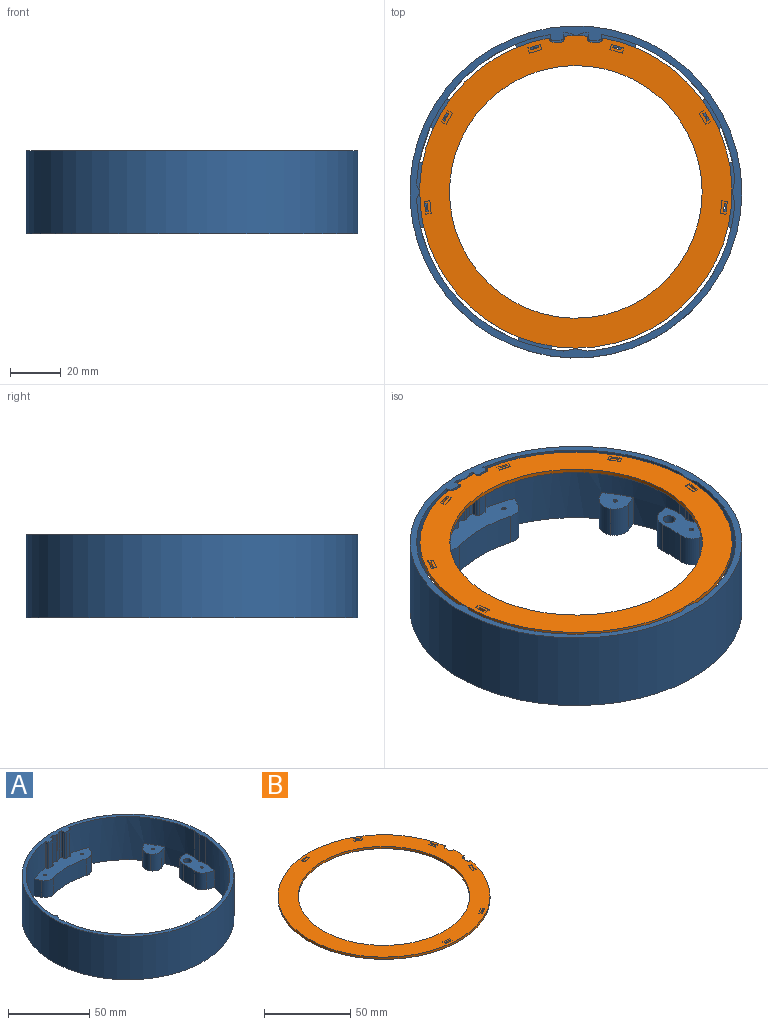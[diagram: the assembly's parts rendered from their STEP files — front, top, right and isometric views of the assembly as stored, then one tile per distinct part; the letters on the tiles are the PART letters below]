
ASSEMBLY  parts=2 mates=1
PART A: 74 faces, bbox 130.8x130.8x32.6 mm
  f0: cylinder r=62.87mm len=57.25mm, axis (0,0,1), area 2296.4mm2, adj f1,f5,f8,f10,f27,f44,f45,f46
  f1: plane 25.87x10.33mm, normal (0,0,1), area 199.3mm2, adj f0,f3,f15,f19,f34,f36,f47,f48
  f2: plane 25.87x10.43mm, normal (0,0,1), area 200.9mm2, adj f3,f4,f12,f22,f35,f38,f41,f55
  f3: cylinder r=62.87mm len=125.47mm, axis (0,0,1), area 5557.1mm2, adj f1,f2,f10,f13,f36,f37,f38,f39
  f4: cylinder r=62.87mm len=58.91mm, axis (0,0,1), area 2329.4mm2, adj f2,f5,f9,f10,f24,f40,f41,f42
  f5: plane 47.77x12.29mm, normal (0,0,1), area 400.8mm2, adj f0,f4,f6,f7,f11,f17,f20,f24
  f6: cylinder r=62.87mm len=19.94mm, axis (0,0,1), area 33.8mm2, adj f5,f25,f60,f73
  f7: cylinder r=62.87mm len=19.94mm, axis (0,0,1), area 33.8mm2, adj f5,f28,f60,f72
  f8: plane 13.34x12.6mm, normal (0,0,1), area 105.4mm2, adj f0,f23,f45,f46,f49,f50
  f9: plane 13.34x12.6mm, normal (0,0,1), area 105.4mm2, adj f4,f21,f40,f42,f52,f53
  f10: plane 130.81x130.81mm, normal (0,0,-1), area 2194.9mm2, adj f0,f3,f4,f11,f12,f14,f15,f16
  f11: cylinder r=52.7mm len=28.54mm, axis (0,0,-1), area 366.3mm2, adj f5,f10,f51,f54
  f12: cylinder r=52.7mm len=12.67mm, axis (0,0,-1), area 126.7mm2, adj f2,f10,f55,f59
  f13: plane 14.43x11.55mm, normal (0,0,1), area 118.3mm2, adj f3,f14,f18,f37,f39,f57,f58
  f14: cylinder r=52.7mm len=12.67mm, axis (0,0,-1), area 11.7mm2, adj f10,f13,f57,f58
  f15: cylinder r=52.7mm len=12.67mm, axis (0,0,-1), area 126.7mm2, adj f1,f10,f48,f56
  f16: cylinder r=65.41mm len=130.81mm, axis (0,0,-1), area 13402.6mm2, adj f10,f60
  f17: cylinder r=0.83mm len=12.67mm, axis (0,0,1), area 65.7mm2, adj f5,f10
  f18: cylinder r=0.83mm len=12.67mm, axis (0,0,1), area 65.7mm2, adj f10,f13
  f19: cylinder r=0.83mm len=12.67mm, axis (0,0,1), area 65.7mm2, adj f1,f10
  f20: cylinder r=0.83mm len=12.67mm, axis (0,0,1), area 65.7mm2, adj f5,f10
  f21: cylinder r=0.83mm len=12.67mm, axis (0,0,1), area 65.7mm2, adj f9,f10
  f22: cylinder r=0.83mm len=12.67mm, axis (0,0,1), area 65.7mm2, adj f2,f10
  f23: cylinder r=0.83mm len=12.67mm, axis (0,0,1), area 65.7mm2, adj f8,f10
  f24: plane 19.94x1.21mm, normal (-1,0,0), area 24mm2, adj f4,f5,f33,f60
  f25: plane 19.94x1.85mm, normal (1,0,0), area 36.8mm2, adj f5,f6,f32,f60
  f26: plane 19.94x3.3mm, normal (0,-1,0), area 65.8mm2, adj f5,f32,f33,f60
  f27: plane 19.94x1.21mm, normal (1,0,0), area 24mm2, adj f0,f5,f31,f60
  f28: plane 19.94x1.85mm, normal (-1,0,0), area 36.8mm2, adj f5,f7,f30,f60
  f29: plane 19.94x3.3mm, normal (0,-1,0), area 65.8mm2, adj f5,f30,f31,f60
  f30: cylinder r=1.02mm len=19.94mm, axis (0,0,1), area 31.8mm2, adj f5,f28,f29,f60
  f31: cylinder r=1.02mm len=19.94mm, axis (0,0,-1), area 31.8mm2, adj f5,f27,f29,f60
  f32: cylinder r=1.02mm len=19.94mm, axis (0,0,1), area 31.8mm2, adj f5,f25,f26,f60
  f33: cylinder r=1.02mm len=19.94mm, axis (0,0,-1), area 31.8mm2, adj f5,f24,f26,f60
  f34: cylinder r=2.35mm len=12.67mm, axis (0,0,1), area 187.1mm2, adj f1,f10
  f35: cylinder r=2.35mm len=12.67mm, axis (0,0,1), area 187.1mm2, adj f2,f10
  f36: plane 12.67x4.78mm, normal (-0.35,-0.94,0), area 64.7mm2, adj f1,f3,f10,f56
  f37: plane 12.67x2.99mm, normal (0.95,-0.31,0), area 39.8mm2, adj f3,f10,f13,f57
  f38: plane 12.67x4.78mm, normal (0.35,-0.94,0), area 64.7mm2, adj f2,f3,f10,f59
  f39: plane 12.67x3.41mm, normal (-0.96,0.28,0), area 44.9mm2, adj f3,f10,f13,f58
  f40: plane 12.67x4.16mm, normal (-0.36,-0.93,0), area 56.6mm2, adj f4,f9,f10,f52
  f41: plane 12.67x4mm, normal (0.17,0.98,0), area 51.4mm2, adj f2,f4,f10,f55
  f42: plane 12.67x3.16mm, normal (0.53,0.85,0), area 47.4mm2, adj f4,f9,f10,f53
  f43: plane 12.67x4.29mm, normal (-0.88,-0.47,0), area 61.7mm2, adj f4,f5,f10,f54
  f44: plane 12.67x4.29mm, normal (0.88,-0.47,0), area 61.7mm2, adj f0,f5,f10,f51
  f45: plane 12.67x3.16mm, normal (-0.53,0.85,0), area 47.4mm2, adj f0,f8,f10,f49
  f46: plane 12.67x4.16mm, normal (0.36,-0.93,0), area 56.6mm2, adj f0,f8,f10,f50
  f47: plane 12.67x4mm, normal (-0.17,0.98,0), area 51.4mm2, adj f0,f1,f10,f48
  f48: cylinder r=6.35mm len=12.67mm, axis (0,0,-1), area 119mm2, adj f1,f10,f15,f47
  f49: cylinder r=6.35mm len=12.67mm, axis (0,0,-1), area 120.7mm2, adj f8,f10,f45,f50
  f50: cylinder r=6.35mm len=12.67mm, axis (0,0,-1), area 111.4mm2, adj f8,f10,f46,f49
  f51: cylinder r=6.35mm len=12.67mm, axis (0,0,-1), area 109mm2, adj f5,f10,f11,f44
  f52: cylinder r=6.35mm len=12.67mm, axis (0,0,-1), area 111.4mm2, adj f9,f10,f40,f53
  f53: cylinder r=6.35mm len=12.67mm, axis (0,0,-1), area 120.7mm2, adj f9,f10,f42,f52
  f54: cylinder r=6.35mm len=12.67mm, axis (0,0,-1), area 109mm2, adj f5,f10,f11,f43
  f55: cylinder r=6.35mm len=12.67mm, axis (0,0,-1), area 119mm2, adj f2,f10,f12,f41
  f56: cylinder r=6.35mm len=12.67mm, axis (0,0,-1), area 106.3mm2, adj f1,f10,f15,f36
  f57: cylinder r=6.35mm len=12.67mm, axis (0,0,-1), area 131.1mm2, adj f10,f13,f14,f37
  f58: cylinder r=6.35mm len=12.67mm, axis (0,0,-1), area 125.7mm2, adj f10,f13,f14,f39
  f59: cylinder r=6.35mm len=12.67mm, axis (0,0,-1), area 106.3mm2, adj f2,f10,f12,f38
  f60: plane 130.81x130.81mm, normal (0,0,1), area 1070.7mm2, adj f0,f3,f4,f6,f7,f16,f24,f25
  f61: cylinder r=1.27mm len=19.94mm, axis (0,0,-1), area 23.9mm2, adj f5,f60,f72,f73
  f62: plane 9.57x1.27mm, normal (0,0,-1), area 5.9mm2, adj f3,f63,f68,f69
  f63: cylinder r=1.27mm len=19.94mm, axis (0,0,-1), area 35.6mm2, adj f60,f62,f68,f69
  f64: cylinder r=1.27mm len=19.94mm, axis (0,0,-1), area 23.9mm2, adj f2,f60,f70,f71
  f65: cylinder r=1.27mm len=19.94mm, axis (0,0,-1), area 35.6mm2, adj f1,f60,f66,f67
  f66: plane 19.94x3.96mm, normal (-0.98,-0.19,0), area 80.6mm2, adj f1,f3,f60,f65
  f67: plane 19.94x3.96mm, normal (-0.98,0.19,0), area 80.6mm2, adj f0,f1,f60,f65
  f68: plane 19.94x3.96mm, normal (-0.19,0.98,0), area 80.6mm2, adj f3,f60,f62,f63
  f69: plane 19.94x3.96mm, normal (0.19,0.98,0), area 80.6mm2, adj f3,f60,f62,f63
  f70: plane 19.94x2.56mm, normal (0.92,0.38,0), area 55.1mm2, adj f2,f4,f60,f64
  f71: plane 19.94x2.56mm, normal (0.92,-0.38,0), area 55.1mm2, adj f2,f3,f60,f64
  f72: plane 19.94x2.56mm, normal (0.38,-0.92,0), area 55.1mm2, adj f5,f7,f60,f61
  f73: plane 19.94x2.56mm, normal (-0.38,-0.92,0), area 55.1mm2, adj f5,f6,f60,f61
PART B: 75 faces, bbox 123.1x123.1x1.7 mm
  f0: plane 123.09x123.09mm, normal (0,0,1), area 4032.5mm2, adj f1,f2,f4,f5,f6,f7,f8,f9
  f1: cylinder r=61.54mm len=123.09mm, axis (0,0,1), area 575.8mm2, adj f0,f3,f5,f23
  f2: cylinder r=61.54mm len=9.02mm, axis (0,0,1), area 14.2mm2, adj f0,f3,f9,f24
  f3: plane 123.09x123.09mm, normal (0,0,-1), area 4077.4mm2, adj f1,f2,f4,f5,f6,f7,f8,f9
  f4: cylinder r=49.76mm len=99.52mm, axis (0,0,1), area 492.3mm2, adj f0,f3
  f5: plane 1.57x0.19mm, normal (0,-1,0), area 0.3mm2, adj f0,f1,f3,f6
  f6: cylinder r=1.45mm len=1.57mm, axis (0,0,-1), area 3.6mm2, adj f0,f3,f5,f7
  f7: plane 3.07x1.57mm, normal (1,0,0), area 4.8mm2, adj f0,f3,f6,f8
  f8: cylinder r=1.45mm len=1.57mm, axis (0,0,-1), area 3.6mm2, adj f0,f3,f7,f9
  f9: plane 1.57x0.93mm, normal (0,1,0), area 1.5mm2, adj f0,f2,f3,f8
  f10: plane 1.7x1.01mm, normal (-0.28,0.96,0), area 1.8mm2, adj f3,f11,f13,f51,f56
  f11: plane 3.17x1.57mm, normal (-0.96,-0.28,0), area 5.2mm2, adj f0,f3,f10,f12
  f12: plane 1.7x1.01mm, normal (0.28,-0.96,0), area 1.8mm2, adj f3,f11,f13,f52,f56
  f13: plane 3.17x1.7mm, normal (0.96,0.28,0), area 5.6mm2, adj f3,f10,f12,f56
  f14: plane 1.7x0.91mm, normal (0.87,-0.5,0), area 1.8mm2, adj f3,f15,f17,f45,f50
  f15: plane 2.86x1.7mm, normal (0.5,0.87,0), area 5.6mm2, adj f3,f14,f16,f50
  f16: plane 1.7x0.91mm, normal (-0.87,0.5,0), area 1.8mm2, adj f3,f15,f17,f49,f50
  f17: plane 2.86x1.65mm, normal (-0.5,-0.87,0), area 5.2mm2, adj f0,f3,f14,f16
  f18: plane 1.7x1.05mm, normal (0.99,0.1,0), area 1.8mm2, adj f3,f19,f21,f43,f44
  f19: plane 3.28x1.7mm, normal (-0.1,0.99,0), area 5.6mm2, adj f3,f18,f20,f44
  f20: plane 1.7x1.05mm, normal (-0.99,-0.1,0), area 1.8mm2, adj f3,f19,f21,f42,f44
  f21: plane 3.28x1.57mm, normal (0.1,-0.99,0), area 5.2mm2, adj f0,f3,f18,f20
  f22: cylinder r=1.45mm len=1.57mm, axis (0,0,-1), area 3.6mm2, adj f0,f3,f23,f26
  f23: plane 1.57x0.19mm, normal (0,1,0), area 0.3mm2, adj f0,f1,f3,f22
  f24: plane 1.57x0.93mm, normal (0,-1,0), area 1.5mm2, adj f0,f2,f3,f25
  f25: cylinder r=1.45mm len=1.57mm, axis (0,0,-1), area 3.6mm2, adj f0,f3,f24,f26
  f26: plane 3.07x1.57mm, normal (1,0,0), area 4.8mm2, adj f0,f3,f22,f25
  f27: plane 1.7x1.01mm, normal (0.28,0.96,0), area 1.8mm2, adj f3,f28,f30,f72,f74
  f28: plane 3.17x1.57mm, normal (-0.96,0.28,0), area 5.2mm2, adj f0,f3,f27,f29
  f29: plane 1.7x1.01mm, normal (-0.28,-0.96,0), area 1.8mm2, adj f3,f28,f30,f73,f74
  f30: plane 3.17x1.7mm, normal (0.96,-0.28,0), area 5.6mm2, adj f3,f27,f29,f74
  f31: plane 1.7x0.91mm, normal (0.87,0.5,0), area 1.8mm2, adj f3,f32,f34,f67,f68
  f32: plane 2.86x1.65mm, normal (-0.5,0.87,0), area 5.2mm2, adj f0,f3,f31,f33
  f33: plane 1.7x0.91mm, normal (-0.87,-0.5,0), area 1.8mm2, adj f3,f32,f34,f63,f68
  f34: plane 2.86x1.7mm, normal (0.5,-0.87,0), area 5.6mm2, adj f3,f31,f33,f68
  f35: plane 1.7x1.05mm, normal (0.99,-0.1,0), area 1.8mm2, adj f3,f36,f38,f57,f62
  f36: plane 3.28x1.57mm, normal (0.1,0.99,0), area 5.2mm2, adj f0,f3,f35,f37
  f37: plane 1.7x1.05mm, normal (-0.99,0.1,0), area 1.8mm2, adj f3,f36,f38,f58,f62
  f38: plane 3.28x1.7mm, normal (-0.1,-0.99,0), area 5.6mm2, adj f3,f35,f37,f62
  f39: plane 2.15x0.23mm, normal (-0.99,-0.1,0), area 0.3mm2, adj f0,f40,f43,f44
  f40: plane 5.05x0.53mm, normal (0.1,-0.99,0), area 0.6mm2, adj f0,f39,f41,f44
  f41: plane 2.15x0.23mm, normal (0.99,0.1,0), area 0.3mm2, adj f0,f40,f42,f44
  f42: plane 0.88x0.13mm, normal (-0.1,0.99,0), area 0.1mm2, adj f0,f20,f41,f44
  f43: plane 0.88x0.13mm, normal (-0.1,0.99,0), area 0.1mm2, adj f0,f18,f39,f44
  f44: plane 5.28x2.68mm, normal (0,0,1), area 7.5mm2, adj f18,f19,f20,f39,f40,f41,f42,f43
  f45: plane 0.77x0.44mm, normal (0.5,0.87,0), area 0.1mm2, adj f0,f14,f46,f50
  f46: plane 1.87x1.08mm, normal (-0.87,0.5,0), area 0.3mm2, adj f0,f45,f47,f50
  f47: plane 4.4x2.54mm, normal (-0.5,-0.87,0), area 0.6mm2, adj f0,f46,f48,f50
  f48: plane 1.87x1.08mm, normal (0.87,-0.5,0), area 0.3mm2, adj f0,f47,f49,f50
  f49: plane 0.77x0.44mm, normal (0.5,0.87,0), area 0.1mm2, adj f0,f16,f48,f50
  f50: plane 5.48x4.41mm, normal (0,0,1), area 7.5mm2, adj f14,f15,f16,f45,f46,f47,f48,f49
  f51: plane 0.85x0.25mm, normal (0.96,0.28,0), area 0.1mm2, adj f0,f10,f55,f56
  f52: plane 0.85x0.25mm, normal (0.96,0.28,0), area 0.1mm2, adj f0,f12,f53,f56
  f53: plane 2.08x0.6mm, normal (-0.28,0.96,0), area 0.3mm2, adj f0,f52,f54,f56
  f54: plane 4.88x1.4mm, normal (-0.96,-0.28,0), area 0.6mm2, adj f0,f53,f55,f56
  f55: plane 2.08x0.6mm, normal (0.28,-0.96,0), area 0.3mm2, adj f0,f51,f54,f56
  f56: plane 5.48x3.48mm, normal (0,0,1), area 7.5mm2, adj f10,f12,f13,f51,f52,f53,f54,f55
  f57: plane 0.88x0.13mm, normal (-0.1,-0.99,0), area 0.1mm2, adj f0,f35,f61,f62
  f58: plane 0.88x0.13mm, normal (-0.1,-0.99,0), area 0.1mm2, adj f0,f37,f59,f62
  f59: plane 2.15x0.23mm, normal (0.99,-0.1,0), area 0.3mm2, adj f0,f58,f60,f62
  f60: plane 5.05x0.53mm, normal (0.1,0.99,0), area 0.6mm2, adj f0,f59,f61,f62
  f61: plane 2.15x0.23mm, normal (-0.99,0.1,0), area 0.3mm2, adj f0,f57,f60,f62
  f62: plane 5.28x2.68mm, normal (0,0,1), area 7.5mm2, adj f35,f37,f38,f57,f58,f59,f60,f61
  f63: plane 0.77x0.44mm, normal (0.5,-0.87,0), area 0.1mm2, adj f0,f33,f64,f68
  f64: plane 1.87x1.08mm, normal (0.87,0.5,0), area 0.3mm2, adj f0,f63,f65,f68
  f65: plane 4.4x2.54mm, normal (-0.5,0.87,0), area 0.6mm2, adj f0,f64,f66,f68
  f66: plane 1.87x1.08mm, normal (-0.87,-0.5,0), area 0.3mm2, adj f0,f65,f67,f68
  f67: plane 0.77x0.44mm, normal (0.5,-0.87,0), area 0.1mm2, adj f0,f31,f66,f68
  f68: plane 5.48x4.41mm, normal (0,0,1), area 7.5mm2, adj f31,f33,f34,f63,f64,f65,f66,f67
  f69: plane 2.08x0.6mm, normal (0.28,0.96,0), area 0.3mm2, adj f0,f70,f73,f74
  f70: plane 4.88x1.4mm, normal (-0.96,0.28,0), area 0.6mm2, adj f0,f69,f71,f74
  f71: plane 2.08x0.6mm, normal (-0.28,-0.96,0), area 0.3mm2, adj f0,f70,f72,f74
  f72: plane 0.85x0.25mm, normal (0.96,-0.28,0), area 0.1mm2, adj f0,f27,f71,f74
  f73: plane 0.85x0.25mm, normal (0.96,-0.28,0), area 0.1mm2, adj f0,f29,f69,f74
  f74: plane 5.48x3.48mm, normal (0,0,1), area 7.5mm2, adj f27,f29,f30,f69,f70,f71,f72,f73
PLACE A t=(26.12,20.74,-13.87)mm
PLACE B rot(axis=(0,0,1),90deg) t=(26.12,20.74,33.38)mm
MATE cylindrical B.f1 <-> A.f0  axis (0,0,1) through (26.12,20.74,33.38)mm
